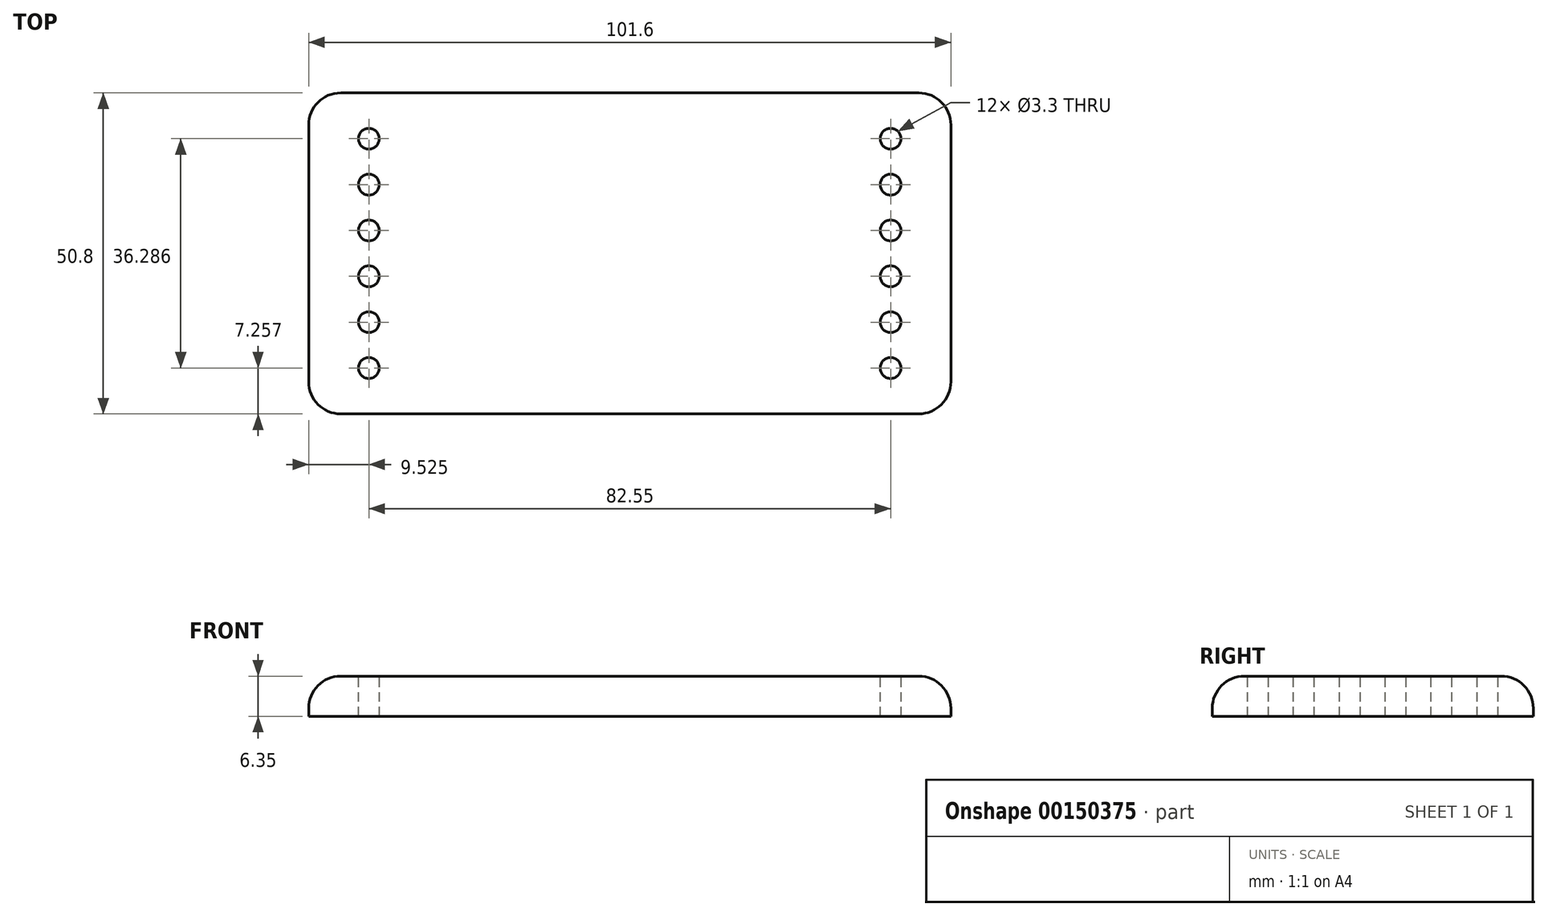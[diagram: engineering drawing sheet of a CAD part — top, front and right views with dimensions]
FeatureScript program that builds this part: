
annotation { "Feature Type Name" : "Feature", "Feature Type Description" : "" }
export const myFeature = defineFeature(function(context is Context, id is Id, definition is map)
    precondition{}
    {
        {
            var Q0;
            Q0=qCreatedBy(makeId("Top.planeOp"),FACE);
            var sketch = newSketch(context, id + "F0", { "sketchPlane" : qUnion([Q0])});
            skLineSegment(sketch, "E0.bottom", {"start": v(50.8, 25.4) * mm, "end": v(-50.8, 25.4) * mm});
            skLineSegment(sketch, "E0.top", {"start": v(50.8, -25.4) * mm, "end": v(-50.8, -25.4) * mm});
            skLineSegment(sketch, "E0.left", {"start": v(50.8, 25.4) * mm, "end": v(50.8, -25.4) * mm});
            skLineSegment(sketch, "E0.right", {"start": v(-50.8, 25.4) * mm, "end": v(-50.8, -25.4) * mm});
            skPoint(sketch, "E0.middle", {"position": v(0, 0) * mm});
            skSolve(sketch);
        }
        {
            var Q0;
            Q0 = qSketchRegion(id + "F0", true);
            extrude(context, id + "F1", {"entities" : qUnion([Q0]), "depth" : 6.35 * mm});
        }
        {
            var Q0;
            Q0=makeQuery(id+"F1.opExtrude","CAP_FACE",FACE,{"disambiguationData":[OSD([sQuery(id+"F0.wireOp",EDGE,"E0.bottom"),sQuery(id+"F0.wireOp",EDGE,"E0.top"),sQuery(id+"F0.wireOp",EDGE,"E0.left"),sQuery(id+"F0.wireOp",EDGE,"E0.right")])],"isStart":false});
            var sketch = newSketch(context, id + "F2", { "sketchPlane" : qUnion([Q0])});
            skCircle(sketch, "E1", {"center": v(-41.28, 10.89) * mm, "radius": 1.65 * mm});
            skCircle(sketch, "E2", {"center": v(-41.28, 3.63) * mm, "radius": 1.65 * mm});
            skCircle(sketch, "E3", {"center": v(-41.28, -3.63) * mm, "radius": 1.65 * mm});
            skCircle(sketch, "E4", {"center": v(-41.28, -10.89) * mm, "radius": 1.65 * mm});
            skCircle(sketch, "E5", {"center": v(-41.28, -18.14) * mm, "radius": 1.65 * mm});
            skCircle(sketch, "E6", {"center": v(-41.28, 18.14) * mm, "radius": 1.65 * mm});
            skLineSegment(sketch, "E7", {"start": v(-41.28, 18.14) * mm, "end": v(-41.28, 10.89) * mm, "construction": true});
            skLineSegment(sketch, "E8", {"start": v(-41.28, 3.63) * mm, "end": v(-41.28, 10.89) * mm, "construction": true});
            skLineSegment(sketch, "E9", {"start": v(-41.28, -3.63) * mm, "end": v(-41.28, 3.63) * mm, "construction": true});
            skLineSegment(sketch, "E10", {"start": v(-41.28, -10.89) * mm, "end": v(-41.28, -3.63) * mm, "construction": true});
            skLineSegment(sketch, "E11", {"start": v(-41.28, -18.14) * mm, "end": v(-41.28, -10.89) * mm, "construction": true});
            skLineSegment(sketch, "E12", {"start": v(-41.28, 0) * mm, "end": v(0, 0) * mm, "construction": true});
            skLineSegment(sketch, "E13", {"start": v(-41.28, 18.14) * mm, "end": v(-41.28, 25.4) * mm, "construction": true});
            skLineSegment(sketch, "E14", {"start": v(-41.28, -18.14) * mm, "end": v(-41.28, -25.4) * mm, "construction": true});
            skCircle(sketch, "E15.MirrorC", {"center": v(41.28, 18.14) * mm, "radius": 1.65 * mm});
            skCircle(sketch, "E16.MirrorC", {"center": v(41.28, 10.89) * mm, "radius": 1.65 * mm});
            skCircle(sketch, "E17.MirrorC", {"center": v(41.28, 3.63) * mm, "radius": 1.65 * mm});
            skCircle(sketch, "E18.MirrorC", {"center": v(41.28, -3.63) * mm, "radius": 1.65 * mm});
            skCircle(sketch, "E19.MirrorC", {"center": v(41.28, -10.89) * mm, "radius": 1.65 * mm});
            skCircle(sketch, "E20.MirrorC", {"center": v(41.28, -18.14) * mm, "radius": 1.65 * mm});
            skSolve(sketch);
        }
        {
            var Q0;
            Q0 = qSketchRegion(id + "F2", true);
            extrude(context, id + "F3", {"entities" : qUnion([Q0]), "operationType" : NewBodyOperationType.REMOVE, "oppositeDirection" : true, "depth" : 25.4 * mm});
        }
        {
            var Q0;
            Q0=makeQuery(id+"F1.opExtrude","SWEPT_EDGE",EDGE,{"disambiguationData":[OSD([sQuery(id+"F0.wireOp",EDGE,"E0.bottom"),sQuery(id+"F0.wireOp",EDGE,"E0.right")])]});
            var Q1;
            Q1=makeQuery(id+"F1.opExtrude","SWEPT_EDGE",EDGE,{"disambiguationData":[OSD([sQuery(id+"F0.wireOp",EDGE,"E0.top"),sQuery(id+"F0.wireOp",EDGE,"E0.right")])]});
            var Q2;
            Q2=makeQuery(id+"F1.opExtrude","SWEPT_EDGE",EDGE,{"disambiguationData":[OSD([sQuery(id+"F0.wireOp",EDGE,"E0.top"),sQuery(id+"F0.wireOp",EDGE,"E0.left")])]});
            var Q3;
            Q3=makeQuery(id+"F1.opExtrude","SWEPT_EDGE",EDGE,{"disambiguationData":[OSD([sQuery(id+"F0.wireOp",EDGE,"E0.bottom"),sQuery(id+"F0.wireOp",EDGE,"E0.left")])]});
            var Q4;
            Q4=makeQuery(id+"F1.opExtrude","CAP_EDGE",EDGE,{"disambiguationData":[OSD([sQuery(id+"F0.wireOp",EDGE,"E0.left")])],"isStart":false});
            var Q5;
            Q5=makeQuery(id+"F1.opExtrude","CAP_EDGE",EDGE,{"disambiguationData":[OSD([sQuery(id+"F0.wireOp",EDGE,"E0.bottom")])],"isStart":false});
            var Q6;
            Q6=makeQuery(id+"F1.opExtrude","CAP_EDGE",EDGE,{"disambiguationData":[OSD([sQuery(id+"F0.wireOp",EDGE,"E0.right")])],"isStart":false});
            var Q7;
            Q7=makeQuery(id+"F1.opExtrude","CAP_EDGE",EDGE,{"disambiguationData":[OSD([sQuery(id+"F0.wireOp",EDGE,"E0.top")])],"isStart":false});
            fillet(context, id + "F4", {"entities" : qUnion([Q0, Q1, Q2, Q3, Q4, Q5, Q6, Q7]), "radius" : 5.08 * mm, "tangentPropagation" : true, "allowEdgeOverflow" : false});
        }
    });
